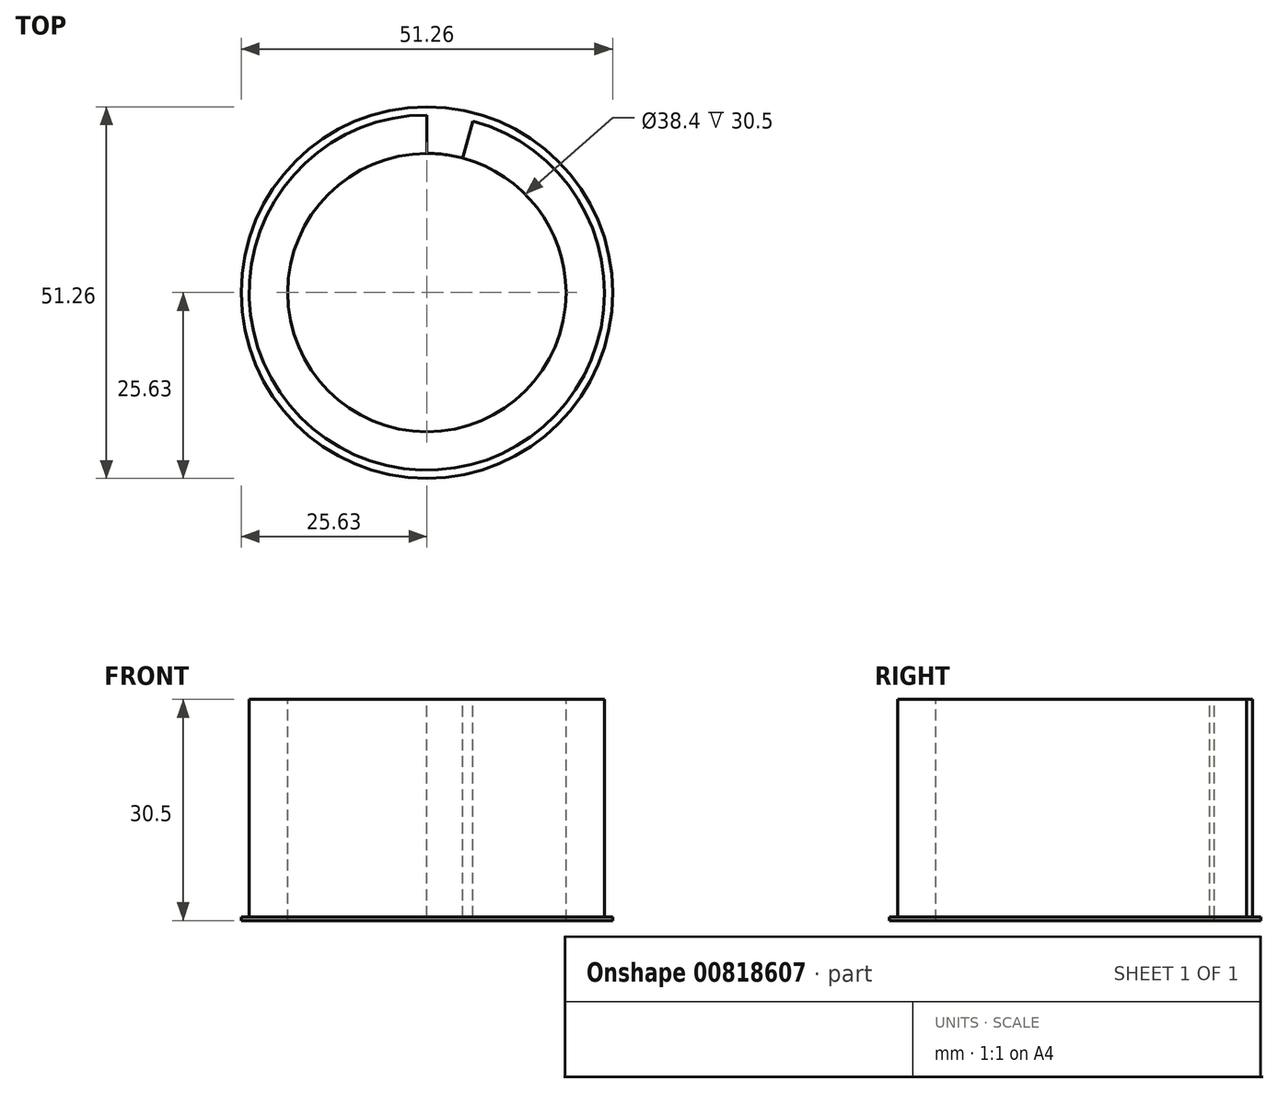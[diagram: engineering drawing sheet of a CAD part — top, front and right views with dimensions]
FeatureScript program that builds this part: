
annotation { "Feature Type Name" : "Feature", "Feature Type Description" : "" }
export const myFeature = defineFeature(function(context is Context, id is Id, definition is map)
    precondition{}
    {
        {
            var Q0;
            Q0=qCreatedBy(makeId("Top.planeOp"),FACE);
            var sketch = newSketch(context, id + "F0", { "sketchPlane" : qUnion([Q0])});
            skCircle(sketch, "E0", {"center": v(0, 0) * mm, "radius": 25.63 * mm});
            skSolve(sketch);
        }
        {
            var Q0;
            Q0 = qSketchRegion(id + "F0", true);
            extrude(context, id + "F1", {"entities" : qUnion([Q0]), "depth" : .5 * mm, "offsetDistance" : 25 * mm});
        }
        {
            var Q0;
            Q0=makeQuery(id+"F1.opExtrude","CAP_FACE",FACE,{"disambiguationData":[OSD([sQuery(id+"F0.wireOp",EDGE,"E0")])],"isStart":false});
            var sketch = newSketch(context, id + "F2", { "sketchPlane" : qUnion([Q0])});
            skCircle(sketch, "E1", {"center": v(0, 0) * mm, "radius": 24.5 * mm});
            skSolve(sketch);
        }
        {
            var Q0;
            Q0 = qSketchRegion(id + "F2", true);
            extrude(context, id + "F3", {"entities" : qUnion([Q0]), "operationType" : NewBodyOperationType.ADD, "depth" : 30 * mm, "offsetDistance" : 25 * mm});
        }
        {
            var Q0;
            Q0=makeQuery(id+"F3.opExtrude","CAP_FACE",FACE,{"disambiguationData":[OSD([sQuery(id+"F2.wireOp",EDGE,"E1")])],"isStart":false});
            var sketch = newSketch(context, id + "F4", { "sketchPlane" : qUnion([Q0])});
            skCircle(sketch, "E2", {"center": v(0, 0) * mm, "radius": 19.2 * mm});
            skSolve(sketch);
        }
        {
            var Q0;
            Q0 = qSketchRegion(id + "F4", true);
            extrude(context, id + "F5", {"entities" : qUnion([Q0]), "operationType" : NewBodyOperationType.REMOVE, "endBound" : BoundingType.THROUGH_ALL, "oppositeDirection" : true, "depth" : 25 * mm, "offsetDistance" : 25 * mm});
        }
        {
            var Q0;
            Q0=makeQuery(id+"F3.opExtrude","CAP_FACE",FACE,{"disambiguationData":[OSD([sQuery(id+"F2.wireOp",EDGE,"E1")])],"isStart":false});
            var sketch = newSketch(context, id + "F6", { "sketchPlane" : qUnion([Q0])});
            skArc(sketch, "E3.0", {"start": v(6.34, 23.67) * mm, "mid": v(3.2, 24.3) * mm, "end": v(0, 24.5) * mm});
            skArc(sketch, "E3.1", {"start": v(4.97, 18.55) * mm, "mid": v(2.5, 19.04) * mm, "end": v(0, 19.2) * mm});
            skLineSegment(sketch, "E4", {"start": v(0, 19.2) * mm, "end": v(0, 24.5) * mm});
            skLineSegment(sketch, "E5", {"start": v(4.97, 18.55) * mm, "end": v(6.34, 23.67) * mm});
            skSolve(sketch);
        }
        {
            var Q0;
            Q0 = qSketchRegion(id + "F6", true);
            var Q1;
            Q1=makeQuery(id+"F1.opExtrude","CAP_FACE",FACE,{"disambiguationData":[OSD([sQuery(id+"F0.wireOp",EDGE,"E0")])],"isStart":false});
            extrude(context, id + "F7", {"entities" : qUnion([Q0]), "operationType" : NewBodyOperationType.REMOVE, "endBound" : BoundingType.UP_TO_SURFACE, "oppositeDirection" : true, "depth" : 25 * mm, "endBoundEntityFace" : qUnion([Q1]), "offsetDistance" : 25 * mm});
        }
    });
